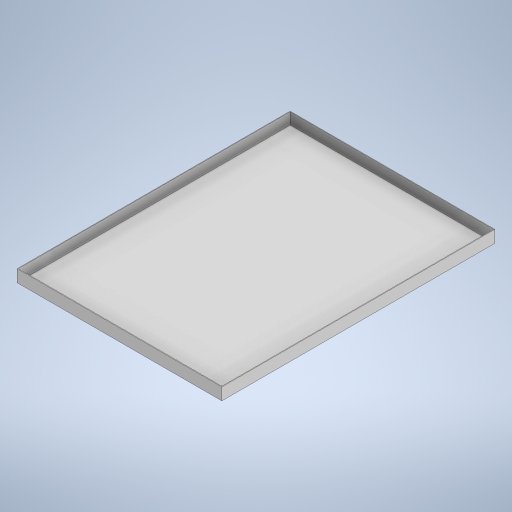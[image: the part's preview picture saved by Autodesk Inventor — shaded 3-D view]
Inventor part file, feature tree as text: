
AUTODESK INVENTOR PART (.ipt)
format: ipt  version: 2024 (Build 280153000, 153)  size: 239,616 bytes
history: native  units: mm
features: extrude x2, sketch x2, other x1
ambient origin geometry x8: Origin, YZ Plane, XZ Plane, XY Plane, X Axis, Y Axis, Z Axis, Center Point
bodies: Body1 (feature_tree)
feature tree (5):
  other  "Sólido1"
  extrude  "Extrusión1"  Depth=1200.0mm
  extrude  "Extrusión2"  Depth=3.0mm
  sketch  "Boceto1"  dims[d0=900.0mm d1=1200.0mm]
  sketch  "Boceto2"  dims[d2=3.0mm d3=0.0mm d4=3.0mm d5=50.0mm d6=0.0mm]
